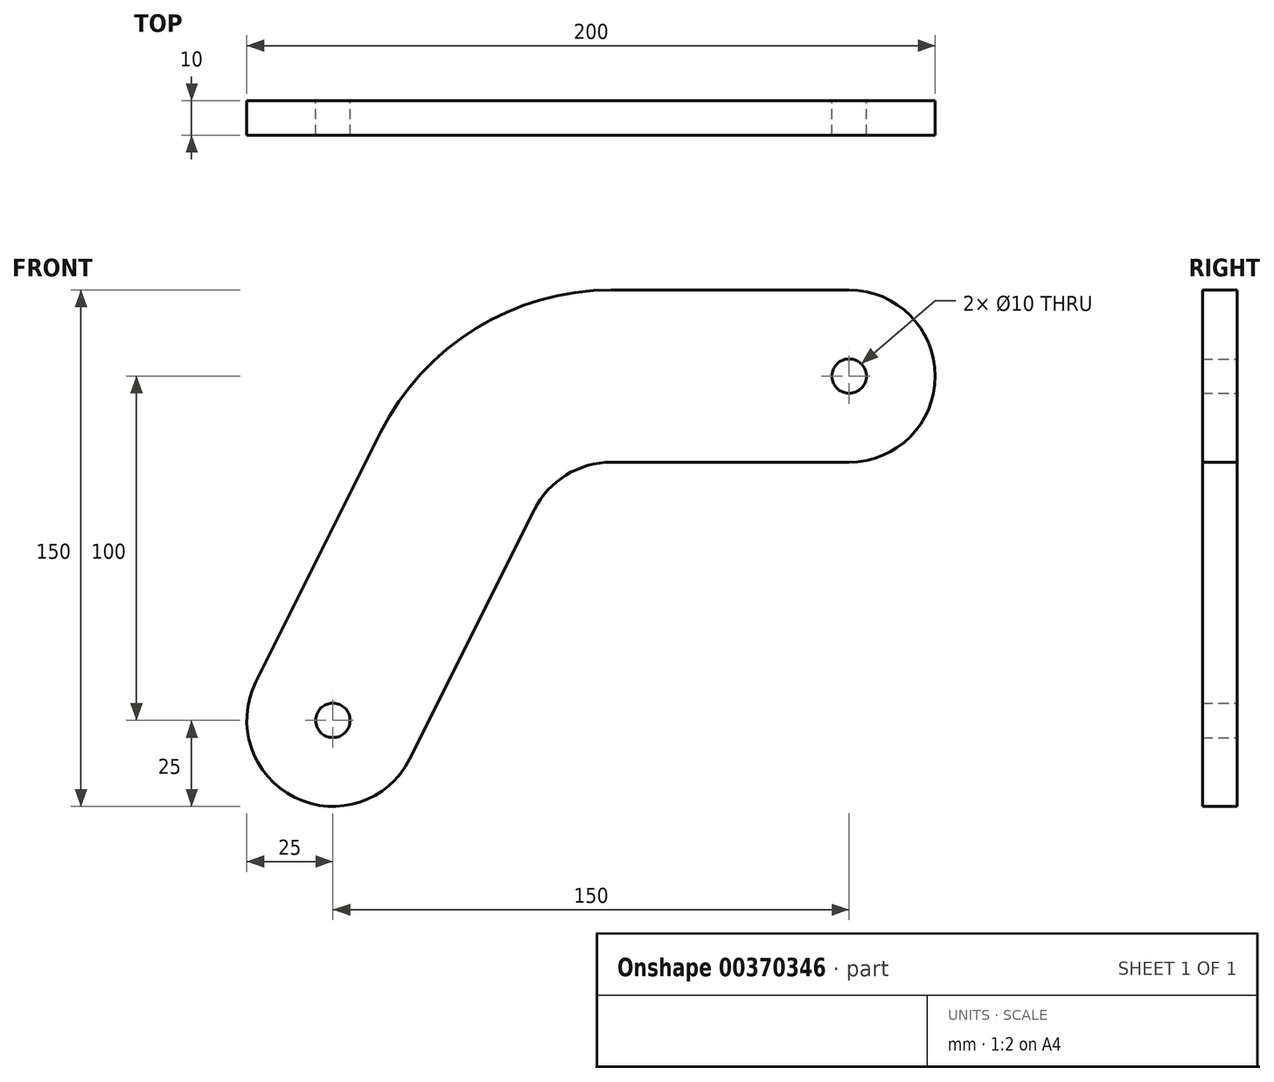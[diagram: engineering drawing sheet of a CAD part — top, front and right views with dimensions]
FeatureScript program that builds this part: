
annotation { "Feature Type Name" : "Feature", "Feature Type Description" : "" }
export const myFeature = defineFeature(function(context is Context, id is Id, definition is map)
    precondition{}
    {
        {
            var Q0;
            Q0=qCreatedBy(makeId("Front.planeOp"),FACE);
            var sketch = newSketch(context, id + "F0", { "sketchPlane" : qUnion([Q0])});
            skArc(sketch, "E0", {"start": v(0, 225) * mm, "mid": v(25, 250) * mm, "end": v(0, 275) * mm});
            skLineSegment(sketch, "E1", {"start": v(-172.36, 161.18) * mm, "end": v(-136.18, 233.54) * mm});
            skArc(sketch, "E2", {"start": v(-127.64, 138.82) * mm, "mid": v(-161.18, 127.64) * mm, "end": v(-172.36, 161.18) * mm});
            skLineSegment(sketch, "E3", {"start": v(-127.64, 138.82) * mm, "end": v(-91.46, 211.18) * mm});
            skLineSegment(sketch, "E4", {"start": v(0, 275) * mm, "end": v(-69.1, 275) * mm});
            skLineSegment(sketch, "E5", {"start": v(0, 225) * mm, "end": v(-69.1, 225) * mm});
            skPoint(sketch, "E6.MirrorCS.start.orphan", {"position": v(-127.64, 138.82) * mm});
            skArc(sketch, "E7", {"start": v(-69.1, 225) * mm, "mid": v(-82.24, 221.27) * mm, "end": v(-91.46, 211.18) * mm});
            skArc(sketch, "E8", {"start": v(-69.1, 275) * mm, "mid": v(-108.53, 263.8) * mm, "end": v(-136.18, 233.54) * mm});
            skPoint(sketch, "E9.end.orphan", {"position": v(-100, 250) * mm});
            skPoint(sketch, "E10.start.orphan", {"position": v(-105.28, 127.64) * mm});
            skCircle(sketch, "E11", {"center": v(-150, 150) * mm, "radius": 5 * mm});
            skCircle(sketch, "E12", {"center": v(0, 250) * mm, "radius": 5 * mm});
            skSolve(sketch);
        }
        {
            var Q0;
            Q0=makeQuery(id+"F0.imprint","IMPRINT",FACE,{"disambiguationData":[TD([[makeQuery(id+"F0.imprint","IMPRINT",EDGE,{"derivedFrom":sQuery(id+"F0.wireOp",EDGE,"E0")}),1.0]])]});
            extrude(context, id + "F1", {"entities" : qUnion([Q0]), "depth" : 10 * mm});
        }
    });
